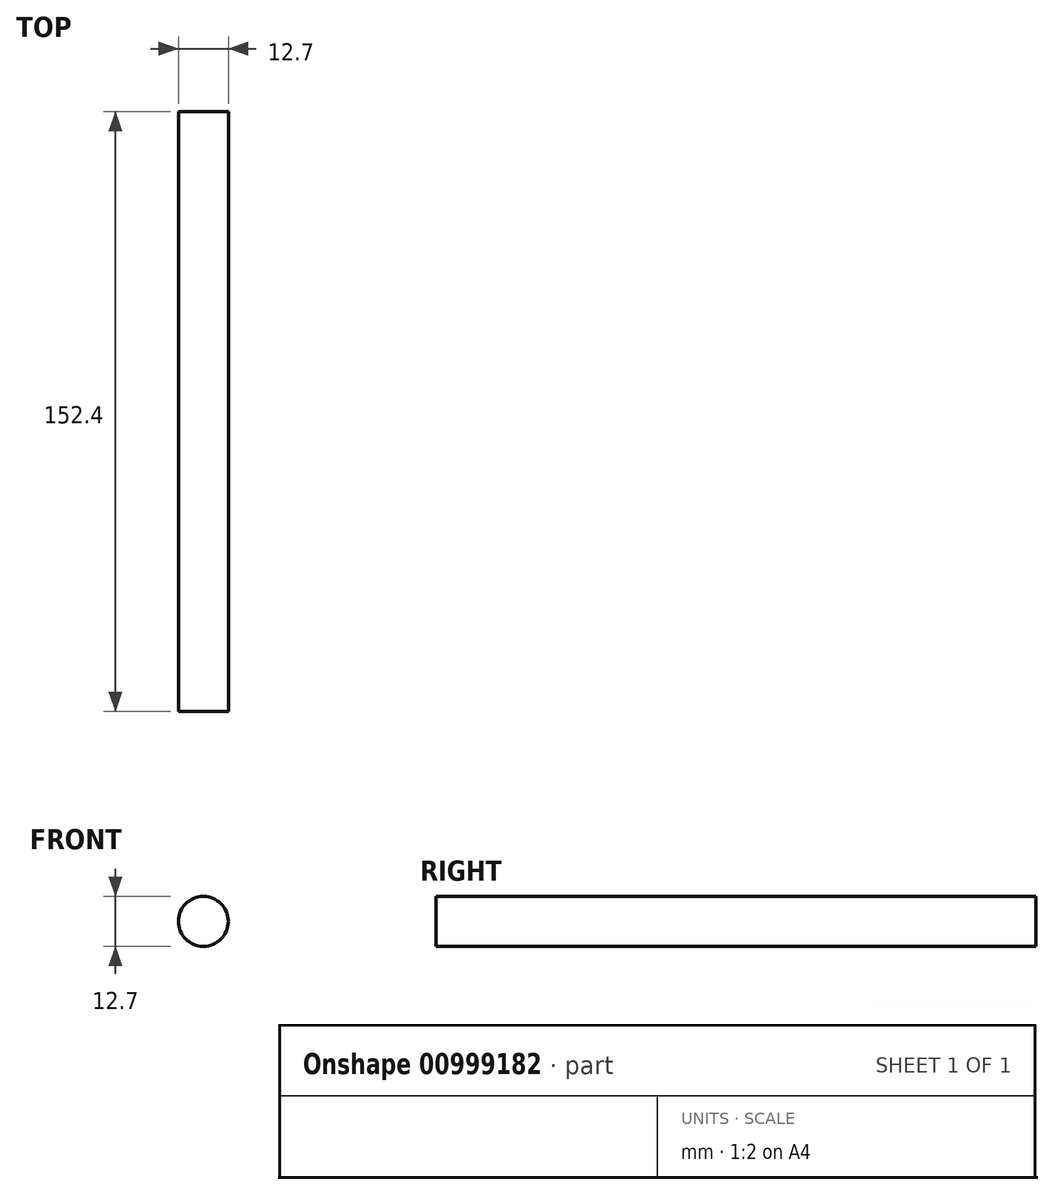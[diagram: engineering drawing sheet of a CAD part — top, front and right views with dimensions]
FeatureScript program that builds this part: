
annotation { "Feature Type Name" : "Feature", "Feature Type Description" : "" }
export const myFeature = defineFeature(function(context is Context, id is Id, definition is map)
    precondition{}
    {
        {
            var Q0;
            Q0=qCreatedBy(makeId("Front.planeOp"),FACE);
            var sketch = newSketch(context, id + "F0", { "sketchPlane" : qUnion([Q0])});
            skCircle(sketch, "E0", {"center": v(0, 0) * mm, "radius": 6.35 * mm});
            skSolve(sketch);
        }
        {
            var Q0;
            Q0=makeQuery(id+"F0.imprint","IMPRINT",FACE,{"disambiguationData":[TD([[makeQuery(id+"F0.imprint","IMPRINT",EDGE,{"derivedFrom":sQuery(id+"F0.wireOp",EDGE,"E0")}),1.0]])]});
            extrude(context, id + "F1", {"entities" : qUnion([Q0]), "depth" : 152.4 * mm, "offsetDistance" : 25.4 * mm});
        }
    });
